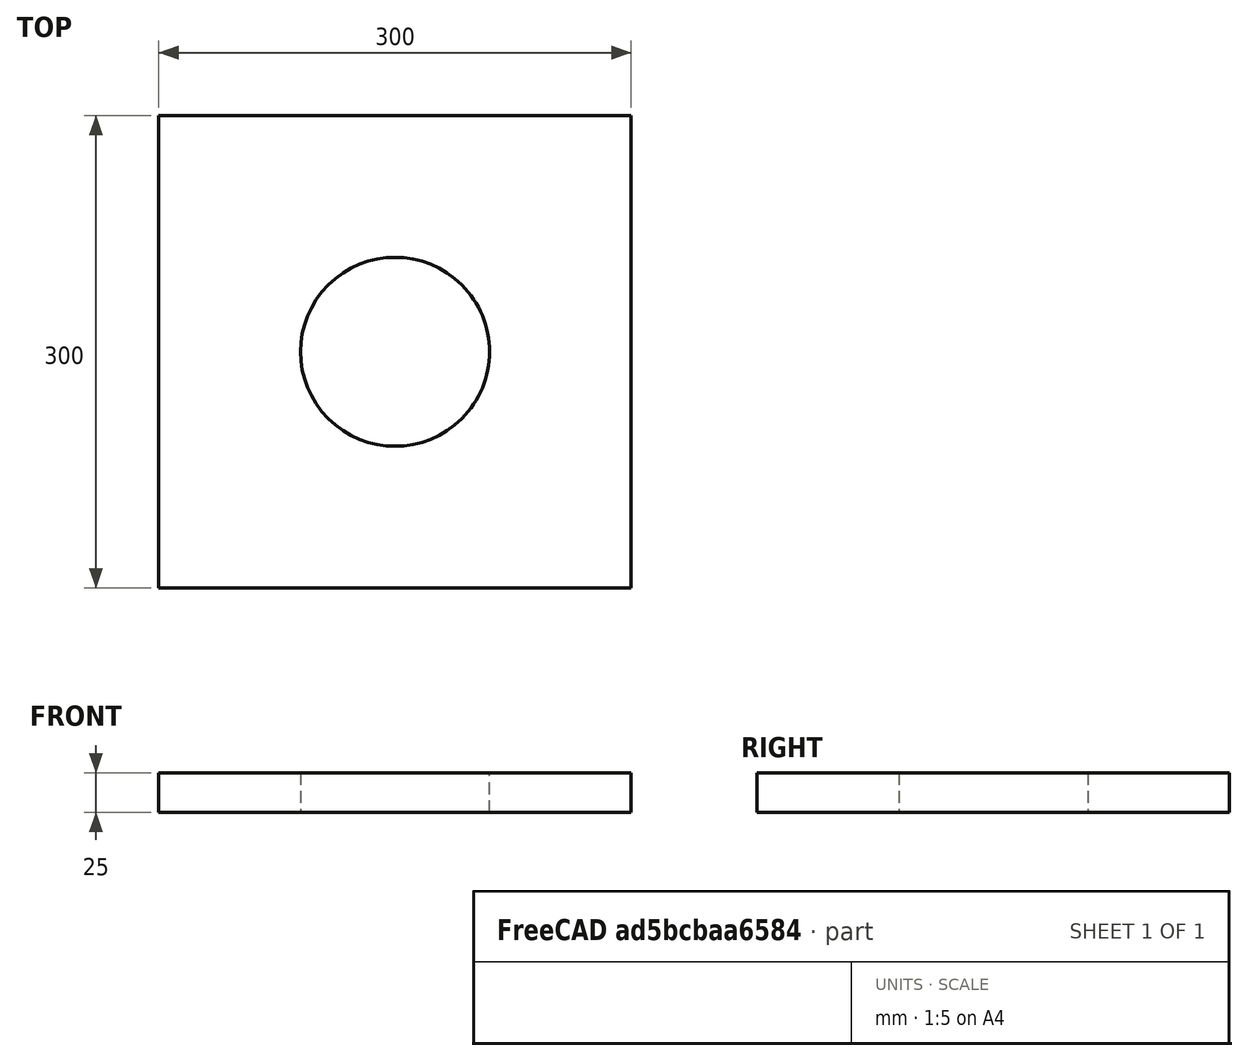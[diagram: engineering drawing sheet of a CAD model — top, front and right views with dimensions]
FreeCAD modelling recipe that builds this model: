
FCSTD DOCUMENT  (FreeCAD 0.21R33694 (Git))
Label: Lug_FaceLoad_Example
License: All rights reserved
LicenseURL: http://en.wikipedia.org/wiki/All_rights_reserved
objects: Part::FeaturePython×5, Sketcher::SketchObject×2, Part::Extrusion×2, Fem::FemSolverObjectPython×1, Fem::ConstraintFixed×1, Part::MultiFuse×1, App::MaterialObjectPython×1, Fem::FemMeshObjectPython×1, Fem::ConstraintForce×1, Fem::FemAnalysis×1
note: 10 computed .brp shape members not serialized (recipe doc carries the construction recipe); baked Part::Feature solids carry a one-line shape summary decoded from their .brp

FEATURE [Sketcher::SketchObject] Sketch
  FullyConstrained = true
  Placement = pos=(150,0,0) rot=(0,0,1;0rad)
  sketch-geometry (5):
    g0: LineSegment StartX=0 StartY=0 StartZ=0 EndX=300 EndY=0 EndZ=0
    g1: LineSegment StartX=300 StartY=0 StartZ=0 EndX=300 EndY=300 EndZ=0
    g2: LineSegment StartX=300 StartY=300 StartZ=0 EndX=0 EndY=300 EndZ=0
    g3: LineSegment StartX=0 StartY=300 StartZ=0 EndX=0 EndY=0 EndZ=0
    g4: Circle CenterX=150 CenterY=150 CenterZ=0 NormalX=0 NormalY=0 NormalZ=1 AngleXU=0 Radius=60
  constraints (14):
    c: Coincident(g0,g1)
    c: Coincident(g1,g2)
    c: Coincident(g2,g3)
    c: Coincident(g3,g0)
    c: Horizontal(g0)
    c: Horizontal(g2)
    c: Vertical(g1)
    c: Vertical(g3)
    c: Coincident(g0,g-1)
    c: DistanceY(g1,g1) = 300
    c: DistanceX(g0,g0) = 300
    c: DistanceX(g0,g4) = 150
    c: DistanceY(g0,g4) = 150
    c: Radius(g4) = 60
FEATURE [Part::Extrusion] Extrude
  Base = -> Sketch
  Dir = (0,0,1)
  DirMode = 2
  FaceMakerClass = Part::FaceMakerBullseye
  LengthFwd = 25
  LengthRev = 0
  Solid = true
  Symmetric = false
FEATURE [Fem::FemSolverObjectPython] SolverCcxTools  # FEM object (typed FeaturePython)
  AnalysisType = 0
  BeamShellResultOutput3D = false
  BucklingFactors = 1
  EigenmodeHighLimit = 1000000
  EigenmodeLowLimit = 0
  EigenmodesCount = 10
  GeometricalNonlinearity = 0
  IterationsControlParameterCutb = 0.25,0.5,0.75,0.85,,,1.5,
  IterationsControlParameterIter = 4,8,9,200,10,400,,200,,
  IterationsControlParameterTimeUse = false
  IterationsThermoMechMaximum = 200
  IterationsUserDefinedIncrementations = false
  IterationsUserDefinedTimeStepLength = false
  MaterialNonlinearity = 0
  MatrixSolverType = 0
  SplitInputWriter = false
  ThermoMechSteadyState = true
  TimeEnd = 1
  TimeInitialStep = 1
FEATURE [Fem::ConstraintFixed] ConstraintFixed001
  NormalDirection = (0,-1,0)
  Normals = (16) [(0,-1,0),(0,-1,0),(0,-1,0),(0,-1,0),(0,-1,0),(0,-1,0),(0,-1,0),(0,-1,0),(0,-1,0),(0,-1,0),(0,-1,0),(0,-1,0),(0,-1,0),(0,-1,0),(0,-1,0),(0,-1,0)]
  Points = (16) [(150,0,25),(250,0,25),(350,0,25),(450,0,25),(150,0,16.6667),(250,0,16.6667),(350,0,16.6667),(450,0,16.6667),(150,0,8.33333),(250,0,8.33333),+6 more]
  References = -> [Extrude]
  Scale = 13
FEATURE [Sketcher::SketchObject] Sketch001
  FullyConstrained = true
  sketch-geometry (2):
    g0: LineSegment StartX=150 StartY=300 StartZ=0 EndX=450 EndY=0 EndZ=0
    g1: LineSegment StartX=150 StartY=0 StartZ=0 EndX=450 EndY=300 EndZ=0
  constraints (8):
    c: DistanceX(g1) = 150
    c: DistanceY(g1,g-1) = 0
    c: DistanceY(g0,g-1) = 0
    c: DistanceX(g1,g0) = 300
    c: DistanceX(g-1,g0) = 150
    c: DistanceX(g-1,g1) = 450
    c: DistanceY(g-1,g0) = 300
    c: DistanceY(g-1,g1) = 300
FEATURE [Part::Extrusion] Extrude001
  Base = -> Sketch001
  Dir = (0,0,1)
  DirMode = 0
  FaceMakerClass = Part::FaceMakerBullseye
  LengthFwd = 25
  LengthRev = 0
  Solid = false
  Symmetric = false
FEATURE [Part::FeaturePython] Slice  # WARN: FeaturePython — macro-defined, semantics opaque (R4)
  Base = -> Extrude
  Mode = 1
  Tolerance = 0
  Tools = -> [Extrude001]
FEATURE [Part::FeaturePython] Slice_child0  label="Slice.0"  # WARN: FeaturePython — macro-defined, semantics opaque (R4)
  Base = -> Slice
  FilterType = 1
  Invert = false
  OverrideMaxVal = 0
  WindowFrom = 80
  WindowTo = 100
  items = 0
FEATURE [Part::FeaturePython] Slice_child1  label="Slice.1"  # WARN: FeaturePython — macro-defined, semantics opaque (R4)
  Base = -> Slice
  FilterType = 1
  Invert = false
  OverrideMaxVal = 0
  WindowFrom = 80
  WindowTo = 100
  items = 1
FEATURE [Part::FeaturePython] Slice_child2  label="Slice.2"  # WARN: FeaturePython — macro-defined, semantics opaque (R4)
  Base = -> Slice
  FilterType = 1
  Invert = false
  OverrideMaxVal = 0
  WindowFrom = 80
  WindowTo = 100
  items = 2
FEATURE [Part::FeaturePython] Slice_child3  label="Slice.3"  # WARN: FeaturePython — macro-defined, semantics opaque (R4)
  Base = -> Slice
  FilterType = 1
  Invert = false
  OverrideMaxVal = 0
  WindowFrom = 80
  WindowTo = 100
  items = 3
FEATURE [Part::MultiFuse] Fusion001  label="Fusion_25mm"
  Shapes = -> [Slice_child0,Slice_child1,Slice_child2,Slice_child3]
FEATURE [App::MaterialObjectPython] MaterialSolid  # material (typed FeaturePython)
  Category = 0
  Material = AuthorAndLicense=(c) 2014 M. Münch - GNU Lesser General Public License (LGPL),CardName=Steel-St-E-315,Density=7800 kg/m^3,Father=Metal,+13 more (map truncated)
FEATURE [Fem::FemMeshObjectPython] FEMMeshGmsh  # FEM object (typed FeaturePython)
  Algorithm2D = 0
  Algorithm3D = 0
  CharacteristicLengthMax = 0
  CharacteristicLengthMin = 0
  CoherenceMesh = true
  ElementDimension = 0
  ElementOrder = 1
  GeometryTolerance = 1e-06
  GroupsOfNodes = false
  HighOrderOptimize = 0
  MeshSizeFromCurvature = 12
  OptimizeNetgen = false
  OptimizeStd = true
  Part = -> Fusion001
  RecombinationAlgorithm = 0
  Recombine3DAll = false
  RecombineAll = false
  SecondOrderLinear = false
FEATURE [Fem::ConstraintForce] ConstraintForce
  Direction = -> Fusion001 [Edge18]
  DirectionVector = (-1,0,0)
  Force = 1000000
  NormalDirection = (1,-1e-16,0)
  Points = (16) [(257.574,192.426,25),(242.044,165.529,25),(242.044,134.471,25),(257.574,107.574,25),(257.574,192.426,16.6667),(242.044,165.529,16.6667),+10 more]
  References = -> [Fusion001]
  Scale = 7
FEATURE [Fem::FemAnalysis] Analysis
  Group = -> [SolverCcxTools,MaterialSolid,ConstraintFixed001,FEMMeshGmsh,ConstraintForce]
